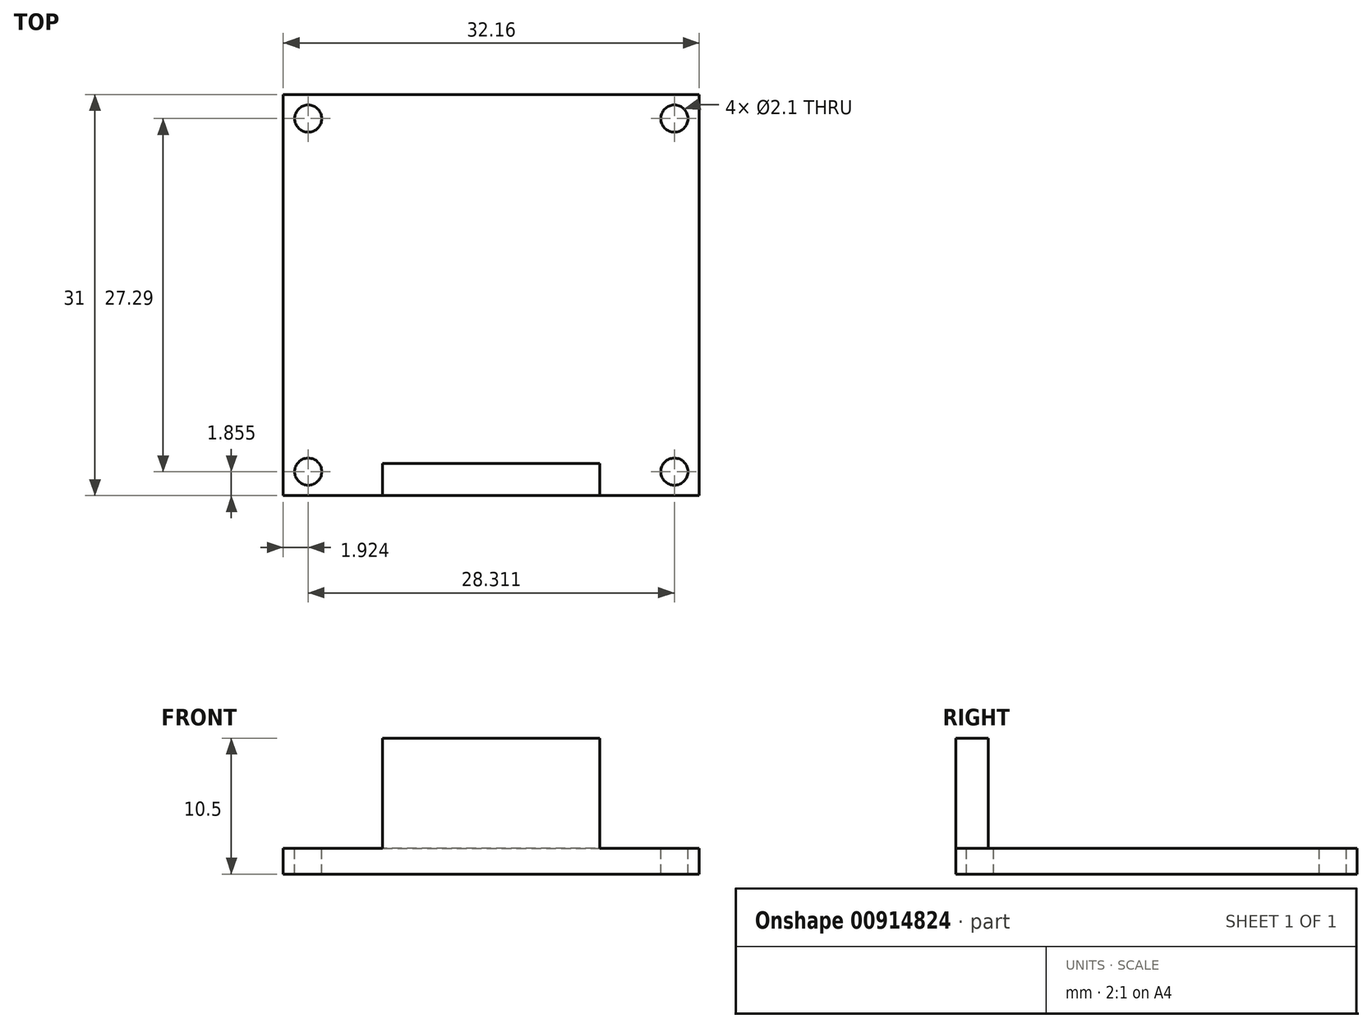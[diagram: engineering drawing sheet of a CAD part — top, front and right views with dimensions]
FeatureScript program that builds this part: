
annotation { "Feature Type Name" : "Feature", "Feature Type Description" : "" }
export const myFeature = defineFeature(function(context is Context, id is Id, definition is map)
    precondition{}
    {
        {
            var Q0;
            Q0=qCreatedBy(makeId("Top.planeOp"),FACE);
            var sketch = newSketch(context, id + "F0", { "sketchPlane" : qUnion([Q0])});
            skLineSegment(sketch, "E0.bottom", {"start": v(16.08, -15.5) * mm, "end": v(-16.08, -15.5) * mm});
            skLineSegment(sketch, "E0.top", {"start": v(16.08, 15.5) * mm, "end": v(-16.08, 15.5) * mm});
            skLineSegment(sketch, "E0.left", {"start": v(16.08, -15.5) * mm, "end": v(16.08, 15.5) * mm});
            skLineSegment(sketch, "E0.right", {"start": v(-16.08, -15.5) * mm, "end": v(-16.08, 15.5) * mm});
            skPoint(sketch, "E0.middle", {"position": v(0, 0) * mm});
            skSolve(sketch);
        }
        {
            var Q0;
            Q0=makeQuery(id+"F0.imprint","IMPRINT",FACE,{"disambiguationData":[TD([[makeQuery(id+"F0.imprint","IMPRINT",EDGE,{"derivedFrom":sQuery(id+"F0.wireOp",EDGE,"E0.bottom")}),-1.0]])]});
            extrude(context, id + "F1", {"entities" : qUnion([Q0]), "depth" : 2 * mm, "offsetDistance" : 25 * mm});
        }
        {
            var Q0;
            Q0=makeQuery(id+"F1.opExtrude","CAP_FACE",FACE,{"disambiguationData":[OSD([sQuery(id+"F0.wireOp",EDGE,"E0.bottom"),sQuery(id+"F0.wireOp",EDGE,"E0.top"),sQuery(id+"F0.wireOp",EDGE,"E0.left"),sQuery(id+"F0.wireOp",EDGE,"E0.right")])],"isStart":false});
            var sketch = newSketch(context, id + "F2", { "sketchPlane" : qUnion([Q0])});
            skLineSegment(sketch, "E1", {"start": v(-16.08, -15.5) * mm, "end": v(16.08, 15.5) * mm});
            skLineSegment(sketch, "E2", {"start": v(16.08, 15.5) * mm, "end": v(16.08, -15.5) * mm});
            skLineSegment(sketch, "E3", {"start": v(16.08, -15.5) * mm, "end": v(-16.08, 15.5) * mm});
            skPoint(sketch, "E4", {"position": v(14.16, 13.64) * mm});
            skPoint(sketch, "E5", {"position": v(-14.16, 13.64) * mm});
            skPoint(sketch, "E6", {"position": v(-14.16, -13.65) * mm});
            skPoint(sketch, "E7", {"position": v(14.16, -13.64) * mm});
            skSolve(sketch);
        }
        {
            var Q0;
            Q0=sQuery(id+"F2.wireOp",VERTEX,"E5");
            var Q1;
            Q1=sQuery(id+"F2.wireOp",VERTEX,"E4");
            var Q2;
            Q2=sQuery(id+"F2.wireOp",VERTEX,"E6");
            var Q3;
            Q3=sQuery(id+"F2.wireOp",VERTEX,"E7");
            var Q4;
            Q4=makeQuery(id+"F1.opExtrude","SWEPT_BODY",BODY,{"disambiguationData":[OSD([sQuery(id+"F0.wireOp",EDGE,"E0.bottom"),sQuery(id+"F0.wireOp",EDGE,"E0.top"),sQuery(id+"F0.wireOp",EDGE,"E0.left"),sQuery(id+"F0.wireOp",EDGE,"E0.right")])]});
            hole(context, id + "F3", {"style" : HoleStyle.SIMPLE, "endStyle" : HoleEndStyle.BLIND, "holeDiameter" : 2.1 * mm, "majorDiameter" : 5 * mm, "holeDepth" : 5 * mm, "isTappedThrough" : true, "tappedDepth" : 12 * mm, "tapClearance" : 3, "startFromSketch" : true, "locations" : qUnion([Q0, Q1, Q2, Q3]), "scope" : qUnion([Q4])});
        }
        {
            var Q0;
            Q0=makeQuery(id+"F1.opExtrude","CAP_FACE",FACE,{"disambiguationData":[OSD([sQuery(id+"F0.wireOp",EDGE,"E0.bottom"),sQuery(id+"F0.wireOp",EDGE,"E0.top"),sQuery(id+"F0.wireOp",EDGE,"E0.left"),sQuery(id+"F0.wireOp",EDGE,"E0.right")])],"isStart":false});
            var sketch = newSketch(context, id + "F4", { "sketchPlane" : qUnion([Q0])});
            skPoint(sketch, "E8", {"position": v(-8.4, -15.5) * mm});
            skPoint(sketch, "E9", {"position": v(0, -15.5) * mm});
            skPoint(sketch, "E10", {"position": v(8.4, -15.5) * mm});
            skPoint(sketch, "E11", {"position": v(8.4, -13) * mm});
            skPoint(sketch, "E12", {"position": v(-5.67, -13) * mm});
            skPoint(sketch, "E13", {"position": v(-8.4, -13) * mm});
            skLineSegment(sketch, "E14", {"start": v(-8.4, -15.5) * mm, "end": v(-8.4, -13) * mm});
            skLineSegment(sketch, "E15", {"start": v(-8.4, -13) * mm, "end": v(8.4, -13) * mm});
            skLineSegment(sketch, "E16", {"start": v(8.4, -13) * mm, "end": v(8.4, -15.5) * mm});
            skSolve(sketch);
        }
        {
            var Q0;
            {var subQ0=sQuery(id+"F4.wireOp",EDGE,"E14");Q0=makeQuery(id+"F4.imprint","IMPRINT",FACE,{"disambiguationData":[TD([[makeQuery(id+"F4.imprint","IMPRINT",EDGE,{"derivedFrom":subQ0}),-1.0]])]});}
            extrude(context, id + "F5", {"entities" : qUnion([Q0]), "operationType" : NewBodyOperationType.ADD, "depth" : 8.5 * mm, "offsetDistance" : 25 * mm});
        }
    });
